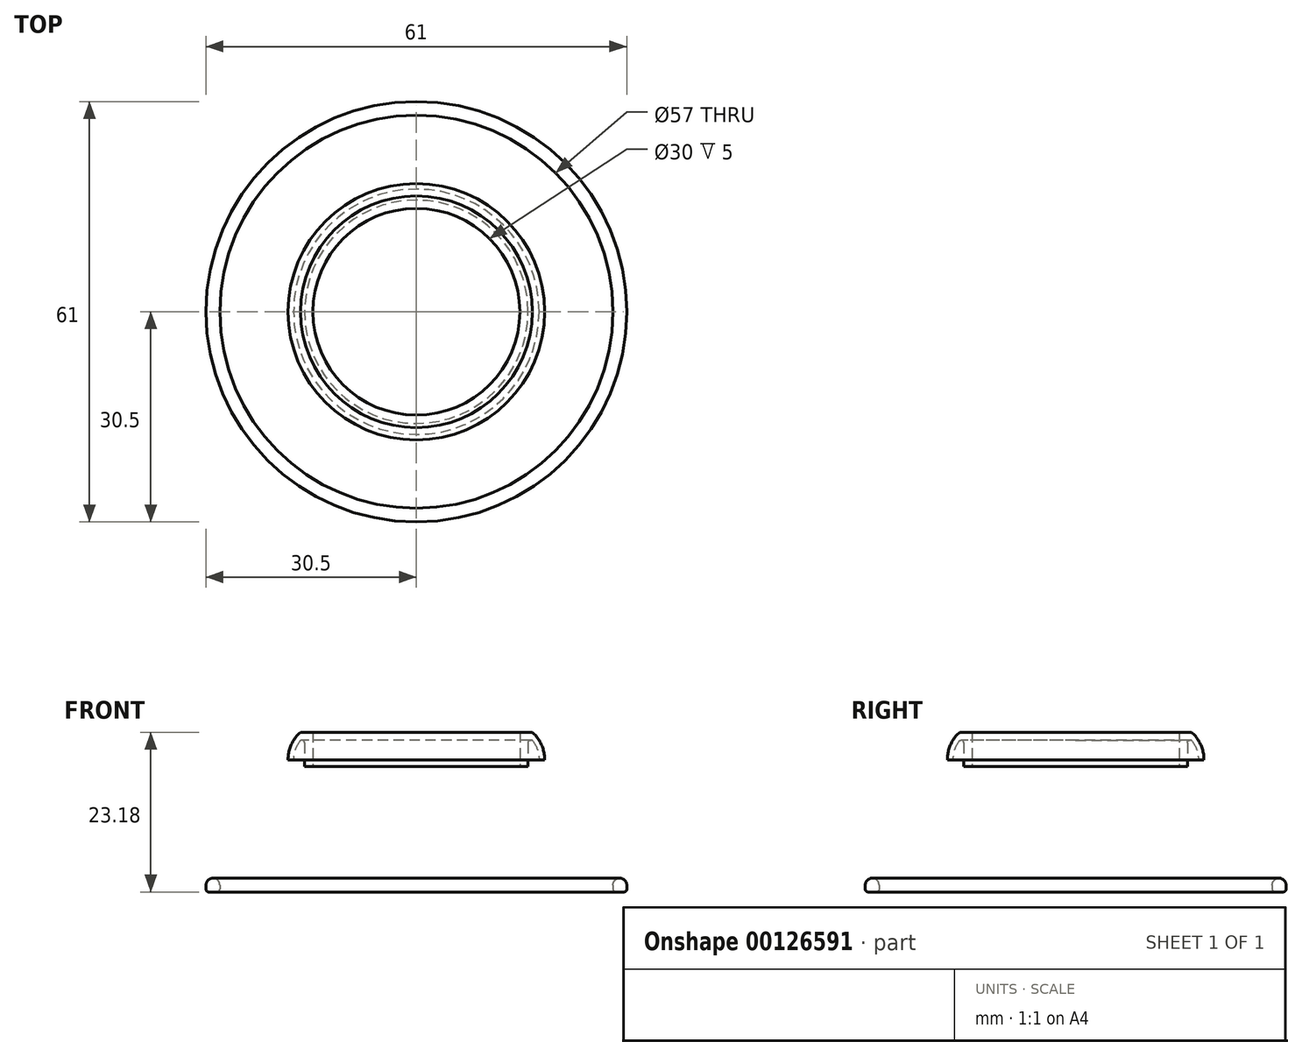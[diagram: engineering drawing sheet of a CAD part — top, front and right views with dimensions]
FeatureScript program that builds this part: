
annotation { "Feature Type Name" : "Feature", "Feature Type Description" : "" }
export const myFeature = defineFeature(function(context is Context, id is Id, definition is map)
    precondition{}
    {
        {
            var Q0;
            Q0=qCreatedBy(makeId("Front.planeOp"),FACE);
            var sketch = newSketch(context, id + "F0", { "sketchPlane" : qUnion([Q0])});
            skArc(sketch, "E0", {"start": v(30.5, 0) * mm, "mid": v(29.5, 1) * mm, "end": v(28.5, 0) * mm});
            skLineSegment(sketch, "E1", {"start": v(0, -3.68) * mm, "end": v(0, 5.6) * mm, "construction": true});
            skLineSegment(sketch, "E2.bottom", {"start": v(28.5, 0) * mm, "end": v(30.5, 0) * mm});
            skLineSegment(sketch, "E2.top", {"start": v(28.5, -1) * mm, "end": v(30.5, -1) * mm});
            skLineSegment(sketch, "E2.left", {"start": v(28.5, 0) * mm, "end": v(28.5, -1) * mm});
            skLineSegment(sketch, "E2.right", {"start": v(30.5, 0) * mm, "end": v(30.5, -1) * mm});
            skLineSegment(sketch, "E3.bottom", {"start": v(15, 17.18) * mm, "end": v(16.2, 17.18) * mm});
            skLineSegment(sketch, "E3.left", {"start": v(15, 17.18) * mm, "end": v(15, 22.18) * mm});
            skLineSegment(sketch, "E3.right", {"start": v(16.2, 17.18) * mm, "end": v(16.2, 21.64) * mm});
            skPoint(sketch, "E4", {"position": v(18.6, 18.18) * mm});
            skLineSegment(sketch, "E5", {"start": v(18.6, 18.18) * mm, "end": v(17.8, 18.18) * mm});
            skLineSegment(sketch, "E6", {"start": v(15, 22.18) * mm, "end": v(16.8, 22.18) * mm});
            skArc(sketch, "E7", {"start": v(18.6, 18.18) * mm, "mid": v(18.13, 20.37) * mm, "end": v(16.8, 22.18) * mm});
            skArc(sketch, "E8", {"start": v(17.8, 18.18) * mm, "mid": v(17.38, 20.09) * mm, "end": v(16.2, 21.64) * mm});
            skSolve(sketch);
        }
        {
            var Q0;
            Q0=makeQuery(id+"F0.imprint","IMPRINT",FACE,{"disambiguationData":[TD([[makeQuery(id+"F0.imprint","IMPRINT",EDGE,{"derivedFrom":sQuery(id+"F0.wireOp",EDGE,"E0")}),1.0]])]});
            var Q1;
            Q1=makeQuery(id+"F0.imprint","IMPRINT",FACE,{"disambiguationData":[TD([[makeQuery(id+"F0.imprint","IMPRINT",EDGE,{"derivedFrom":sQuery(id+"F0.wireOp",EDGE,"E2.bottom")}),-1.0]])]});
            var Q2;
            Q2=makeQuery(id+"F0.imprint","IMPRINT",FACE,{"disambiguationData":[TD([[makeQuery(id+"F0.imprint","IMPRINT",EDGE,{"derivedFrom":sQuery(id+"F0.wireOp",EDGE,"E3.bottom")}),1.0]])]});
            var Q3;
            Q3=sQuery(id+"F0.wireOp",EDGE,"E1");
            revolve(context, id + "F1", {"entities" : qUnion([Q0, Q1, Q2]), "axis" : qUnion([Q3]), "revolveType" : RevolveType.FULL});
        }
        {
            var Q0;
            Q0=makeQuery(id+"F1.opRevolve","SWEPT_EDGE",EDGE,{"disambiguationData":[OSD([sQuery(id+"F0.wireOp",EDGE,"E2.top"),sQuery(id+"F0.wireOp",EDGE,"E2.left")])]});
            var Q1;
            Q1=makeQuery(id+"F1.opRevolve","SWEPT_EDGE",EDGE,{"disambiguationData":[OSD([sQuery(id+"F0.wireOp",EDGE,"E2.top"),sQuery(id+"F0.wireOp",EDGE,"E2.right")])]});
            fillet(context, id + "F2", {"entities" : qUnion([Q0, Q1]), "radius" : 0.4 * mm, "tangentPropagation" : true, "allowEdgeOverflow" : false});
        }
        {
            var Q0;
            Q0=makeQuery(id+"F1.opRevolve","SWEPT_EDGE",EDGE,{"disambiguationData":[OSD([sQuery(id+"F0.wireOp",EDGE,"E3.right"),sQuery(id+"F0.wireOp",EDGE,"E8")])]});
            fillet(context, id + "F3", {"entities" : qUnion([Q0]), "radius" : 0.4 * mm, "tangentPropagation" : true, "allowEdgeOverflow" : false});
        }
    });
